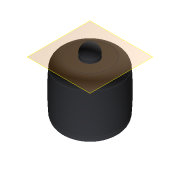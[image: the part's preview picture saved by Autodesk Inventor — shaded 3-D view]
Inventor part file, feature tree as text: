
AUTODESK INVENTOR PART (.ipt)
format: ipt  version: 2017 (Build 210142000, 142)  size: 150,528 bytes
history: native  units: mm
features: sketch x3, fillet x3, mirror x2, plane x1, loft x1, extrude x1, thicken_offset x1
ambient origin geometry x8: Origin, YZ Plane, XZ Plane, XY Plane, X Axis, Y Axis, Z Axis, Center Point
bodies: Solid1 (feature_tree)
feature tree (12):
  sketch  "Sketch1"  dims[d0=12.0mm d1=6.0mm d2=10.5mm d3=0.0mm d4=90.0deg]
  plane  "Work Plane1"
  loft  "Loft1"
  mirror  "Mirror1"
  fillet  "Fillet1"  Radius=10.5mm
  fillet  "Fillet2"  [1 undecoded]
  extrude  "Extrusion1"  Depth=2.0mm
  fillet  "Fillet3"  Radius=2.0mm
  mirror  "Mirror2"
  thicken_offset  "Thicken1"
  sketch  "Sketch2"  dims[d5=0.0mm d6=90.0deg d7=50.0mm d8=2.0mm]
  sketch  "Sketch3"  dims[d9=3.5mm d10=2.5mm d11=0.0mm d12=1.75mm d13=0.75mm d14=0.5mm]
note: 1 required parameter value undecoded (feature->parameter linkage not recoverable at this tier; creation-order binding heuristic only, values carry confidence <= 0.55)
